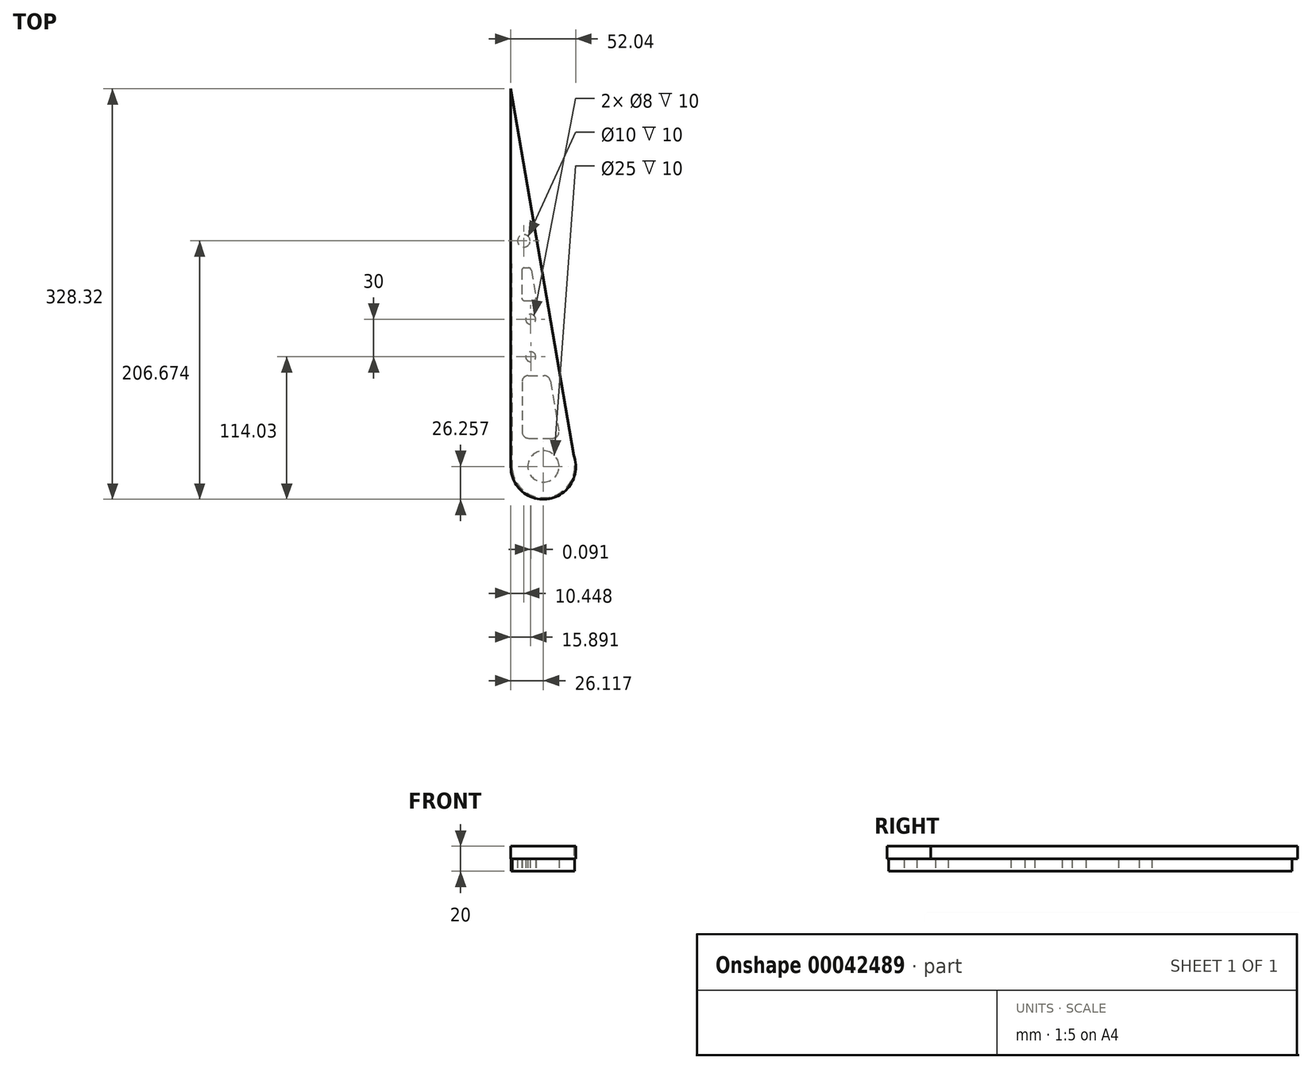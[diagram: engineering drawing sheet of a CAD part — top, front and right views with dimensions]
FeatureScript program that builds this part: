
annotation { "Feature Type Name" : "Feature", "Feature Type Description" : "" }
export const myFeature = defineFeature(function(context is Context, id is Id, definition is map)
    precondition{}
    {
        {
            var Q0;
            Q0=qCreatedBy(makeId("Top.planeOp"),FACE);
            var sketch = newSketch(context, id + "F0", { "sketchPlane" : qUnion([Q0])});
            skLineSegment(sketch, "E0", {"start": v(-19.63, -57.7) * mm, "end": v(-20.54, 242.3) * mm});
            skArc(sketch, "E1", {"start": v(-19.63, -57.7) * mm, "mid": v(8.6, -79.95) * mm, "end": v(29.85, -50.96) * mm});
            skPoint(sketch, "E1.second.point", {"position": v(-6.38, -77.32) * mm});
            skPoint(sketch, "E1.third.point", {"position": v(23.08, -37.7) * mm});
            skLineSegment(sketch, "E2", {"start": v(-20.54, 242.3) * mm, "end": v(29.85, -50.96) * mm});
            skCircle(sketch, "E3", {"center": v(5.23, -55.2) * mm, "radius": 12.5 * mm});
            skLineSegment(sketch, "E4", {"start": v(-10.05, 77.5) * mm, "end": v(-2.71, 77.5) * mm});
            skPoint(sketch, "E5.start.orphan", {"position": v(-20.09, 92.3) * mm});
            skCircle(sketch, "E6", {"center": v(-10.44, 125.22) * mm, "radius": 5 * mm});
            skLineSegment(sketch, "E7", {"start": v(-10.12, 103.63) * mm, "end": v(-6.52, 103.63) * mm});
            skLineSegment(sketch, "E8", {"start": v(-12.12, 101.62) * mm, "end": v(-12.05, 79.5) * mm});
            skLineSegment(sketch, "E9", {"start": v(-6.73, -32.62) * mm, "end": v(12.65, -32.62) * mm});
            skPoint(sketch, "E10.orphan", {"position": v(20.45, -43.47) * mm});
            skLineSegment(sketch, "E11.trimOffspring", {"start": v(10.68, 13.35) * mm, "end": v(17.58, -26.77) * mm});
            skPoint(sketch, "E12.orphan", {"position": v(4.75, 47.86) * mm});
            skLineSegment(sketch, "E13.trimOffspring", {"start": v(-11.85, 12.48) * mm, "end": v(-11.73, -27.63) * mm});
            skLineSegment(sketch, "E14.trimOffspring", {"start": v(-6.85, 17.5) * mm, "end": v(5.76, 17.5) * mm});
            skLineSegment(sketch, "E15.trimOffspring", {"start": v(-4.54, 101.96) * mm, "end": v(-0.74, 79.84) * mm});
            skPoint(sketch, "E16.orphan", {"position": v(-10.94, 139.18) * mm});
            skPoint(sketch, "E17.visualSharp", {"position": v(-11.71, -32.62) * mm});
            skArc(sketch, "E17.filletArc", {"start": v(-11.73, -27.63) * mm, "mid": v(-10.26, -31.16) * mm, "end": v(-6.73, -32.62) * mm});
            skPoint(sketch, "E18.visualSharp", {"position": v(18.58, -32.62) * mm});
            skArc(sketch, "E18.filletArc", {"start": v(12.65, -32.62) * mm, "mid": v(16.47, -30.84) * mm, "end": v(17.58, -26.77) * mm});
            skPoint(sketch, "E19.visualSharp", {"position": v(-11.86, 17.5) * mm});
            skArc(sketch, "E19.filletArc", {"start": v(-6.85, 17.5) * mm, "mid": v(-10.39, 16.03) * mm, "end": v(-11.85, 12.48) * mm});
            skPoint(sketch, "E20.visualSharp", {"position": v(9.97, 17.5) * mm});
            skArc(sketch, "E20.filletArc", {"start": v(10.68, 13.35) * mm, "mid": v(8.98, 16.32) * mm, "end": v(5.76, 17.5) * mm});
            skPoint(sketch, "E21.visualSharp", {"position": v(-4.83, 103.63) * mm});
            skArc(sketch, "E21.filletArc", {"start": v(-4.54, 101.96) * mm, "mid": v(-5.23, 103.15) * mm, "end": v(-6.52, 103.63) * mm});
            skPoint(sketch, "E22.visualSharp", {"position": v(-12.12, 103.63) * mm});
            skArc(sketch, "E22.filletArc", {"start": v(-10.12, 103.63) * mm, "mid": v(-11.53, 103.04) * mm, "end": v(-12.12, 101.62) * mm});
            skPoint(sketch, "E23.visualSharp", {"position": v(-12.04, 77.5) * mm});
            skArc(sketch, "E23.filletArc", {"start": v(-12.05, 79.5) * mm, "mid": v(-11.46, 78.08) * mm, "end": v(-10.05, 77.5) * mm});
            skPoint(sketch, "E24.visualSharp", {"position": v(-0.34, 77.5) * mm});
            skArc(sketch, "E24.filletArc", {"start": v(-2.71, 77.5) * mm, "mid": v(-1.18, 78.21) * mm, "end": v(-0.74, 79.84) * mm});
            skLineSegment(sketch, "E25", {"start": v(-5.04, 75.08) * mm, "end": v(-4.88, 22.28) * mm, "construction": true});
            skCircle(sketch, "E26", {"center": v(-5, 62.58) * mm, "radius": 4 * mm});
            skCircle(sketch, "E27", {"center": v(-4.9, 32.58) * mm, "radius": 4 * mm});
            skSolve(sketch);
        }
        {
            var Q0;
            Q0=qSketchRegion(id+"F0",true);
            extrude(context, id + "F1", {"entities" : qUnion([Q0]), "endBound" : BoundingType.SYMMETRIC, "depth" : 20 * mm});
        }
        {
            var Q0;
            Q0=qCreatedBy(makeId("Top.planeOp"),FACE);
            var sketch = newSketch(context, id + "F2", { "sketchPlane" : qUnion([Q0])});
            skLineSegment(sketch, "E28", {"start": v(-12.33, 113.45) * mm, "end": v(-12.33, -47.83) * mm});
            skLineSegment(sketch, "E29", {"start": v(-7.25, 142.54) * mm, "end": v(23.65, -54.83) * mm});
            skLineSegment(sketch, "E30", {"start": v(-12.33, 142.54) * mm, "end": v(-7.25, 142.54) * mm});
            skArc(sketch, "E31", {"start": v(-12.33, -47.83) * mm, "mid": v(1.18, -74.37) * mm, "end": v(23.65, -54.83) * mm});
            skPoint(sketch, "E32.orphan", {"position": v(-12.33, -54.83) * mm});
            skLineSegment(sketch, "E33", {"start": v(-12.33, 113.45) * mm, "end": v(-17.76, 116.29) * mm});
            skLineSegment(sketch, "E34", {"start": v(-17.76, 116.29) * mm, "end": v(-12.33, 142.54) * mm});
            skSolve(sketch);
        }
        {
            var Q0;
            Q0=qSketchRegion(id+"F2",true);
            extrude(context, id + "F3", {"entities" : qUnion([Q0]), "operationType" : NewBodyOperationType.ADD, "depth" : 10 * mm});
        }
        {
            var Q0;
            Q0=qCreatedBy(makeId("Top.planeOp"),FACE);
            var sketch = newSketch(context, id + "F4", { "sketchPlane" : qUnion([Q0])});
            skCircle(sketch, "E35", {"center": v(5.15, -55.45) * mm, "radius": 26 * mm});
            skLineSegment(sketch, "E36", {"start": v(-20.89, 246.87) * mm, "end": v(-20.85, -55.46) * mm});
            skLineSegment(sketch, "E37", {"start": v(-20.25, 111.25) * mm, "end": v(-20.25, 103.43) * mm});
            skLineSegment(sketch, "E38", {"start": v(-20.89, 246.87) * mm, "end": v(31.14, -55.9) * mm});
            skSolve(sketch);
        }
        {
            var Q0;
            Q0 = qSketchRegion(id + "F4", true);
            extrude(context, id + "F5", {"entities" : qUnion([Q0]), "operationType" : NewBodyOperationType.ADD, "depth" : 10 * mm});
        }
    });
